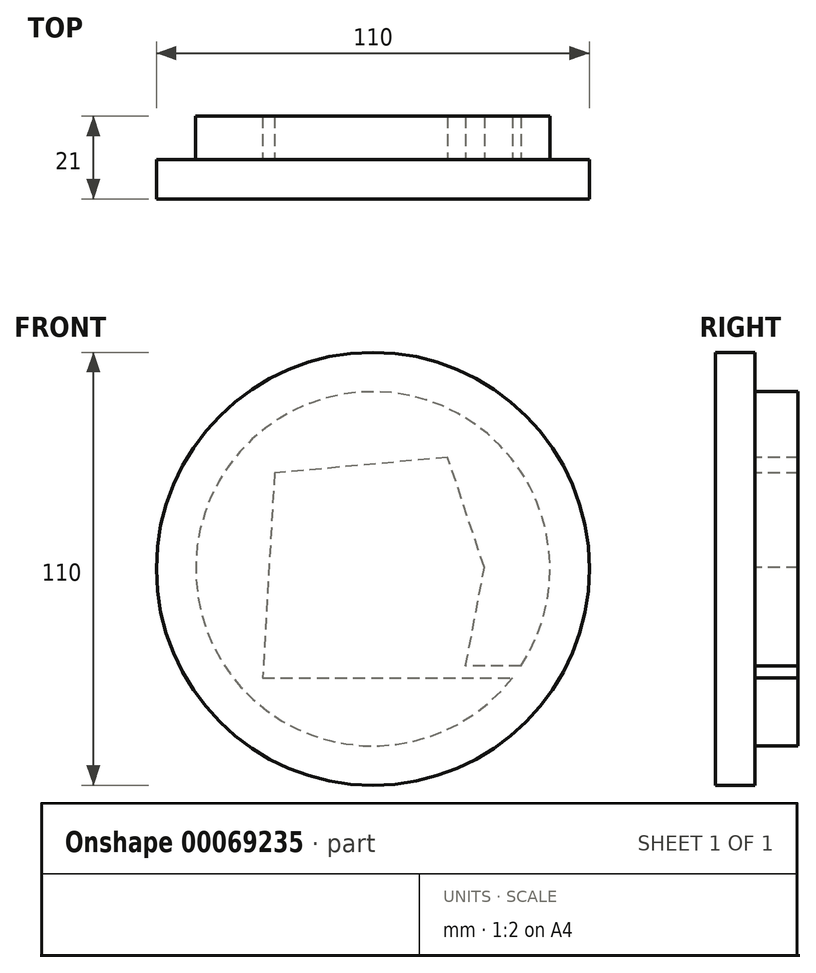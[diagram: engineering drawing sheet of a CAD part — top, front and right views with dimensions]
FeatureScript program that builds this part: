
annotation { "Feature Type Name" : "Feature", "Feature Type Description" : "" }
export const myFeature = defineFeature(function(context is Context, id is Id, definition is map)
    precondition{}
    {
        {
            var Q0;
            Q0=qCreatedBy(makeId("Front.planeOp"),FACE);
            var sketch = newSketch(context, id + "F0", { "sketchPlane" : qUnion([Q0])});
            skLineSegment(sketch, "E0", {"start": v(0, 0) * mm, "end": v(51, 0) * mm});
            skArc(sketch, "E1", {"start": v(65.63, 3) * mm, "mid": v(-8.59, 53.88) * mm, "end": v(63.48, 0) * mm});
            skLineSegment(sketch, "E2", {"start": v(51.57, 3) * mm, "end": v(56.33, 28) * mm});
            skLineSegment(sketch, "E3", {"start": v(56.33, 28) * mm, "end": v(47, 56) * mm});
            skLineSegment(sketch, "E4", {"start": v(47, 56) * mm, "end": v(3, 52) * mm});
            skLineSegment(sketch, "E5", {"start": v(3, 52) * mm, "end": v(0, 0) * mm});
            skPoint(sketch, "E6.orphan", {"position": v(0, 56) * mm});
            skPoint(sketch, "E7.end.orphan", {"position": v(56, 55.35) * mm});
            skPoint(sketch, "E8.orphan", {"position": v(56, 0) * mm});
            skPoint(sketch, "E9.start.orphan", {"position": v(0, 52) * mm});
            skLineSegment(sketch, "E10", {"start": v(51, 0) * mm, "end": v(63.48, 0) * mm});
            skLineSegment(sketch, "E11", {"start": v(65.63, 3) * mm, "end": v(51.57, 3) * mm});
            skLineSegment(sketch, "E12", {"start": v(51.57, 3) * mm, "end": v(65.63, 3) * mm});
            skPoint(sketch, "E13.end.orphan", {"position": v(71.64, 3) * mm});
            skPoint(sketch, "E14.orphan", {"position": v(71.64, 0) * mm});
            skCircle(sketch, "E15", {"center": v(28, 27.68) * mm, "radius": 45 * mm});
            skCircle(sketch, "E16", {"center": v(28, 27.68) * mm, "radius": 55 * mm});
            skSolve(sketch);
        }
        {
            var Q0;
            Q0=makeQuery(id+"F0.imprint","IMPRINT",FACE,{"disambiguationData":[TD([[makeQuery(id+"F0.imprint","IMPRINT",EDGE,{"derivedFrom":sQuery(id+"F0.wireOp",EDGE,"E16")}),1.0]])]});
            var Q1;
            Q1=makeQuery(id+"F0.imprint","IMPRINT",FACE,{"disambiguationData":[TD([[makeQuery(id+"F0.imprint","IMPRINT",EDGE,{"derivedFrom":sQuery(id+"F0.wireOp",EDGE,"E0")}),-1.0]])]});
            var Q2;
            Q2=makeQuery(id+"F0.imprint","IMPRINT",FACE,{"disambiguationData":[TD([[makeQuery(id+"F0.imprint","IMPRINT",EDGE,{"derivedFrom":sQuery(id+"F0.wireOp",EDGE,"E0")}),1.0]])]});
            extrude(context, id + "F1", {"entities" : qUnion([Q0, Q1, Q2]), "depth" : 10 * mm});
        }
        {
            var Q0;
            Q0=makeQuery(id+"F0.imprint","IMPRINT",FACE,{"disambiguationData":[TD([[makeQuery(id+"F0.imprint","IMPRINT",EDGE,{"derivedFrom":sQuery(id+"F0.wireOp",EDGE,"E0")}),-1.0]])]});
            extrude(context, id + "F2", {"entities" : qUnion([Q0]), "operationType" : NewBodyOperationType.ADD, "oppositeDirection" : true, "depth" : 11 * mm});
        }
    });
